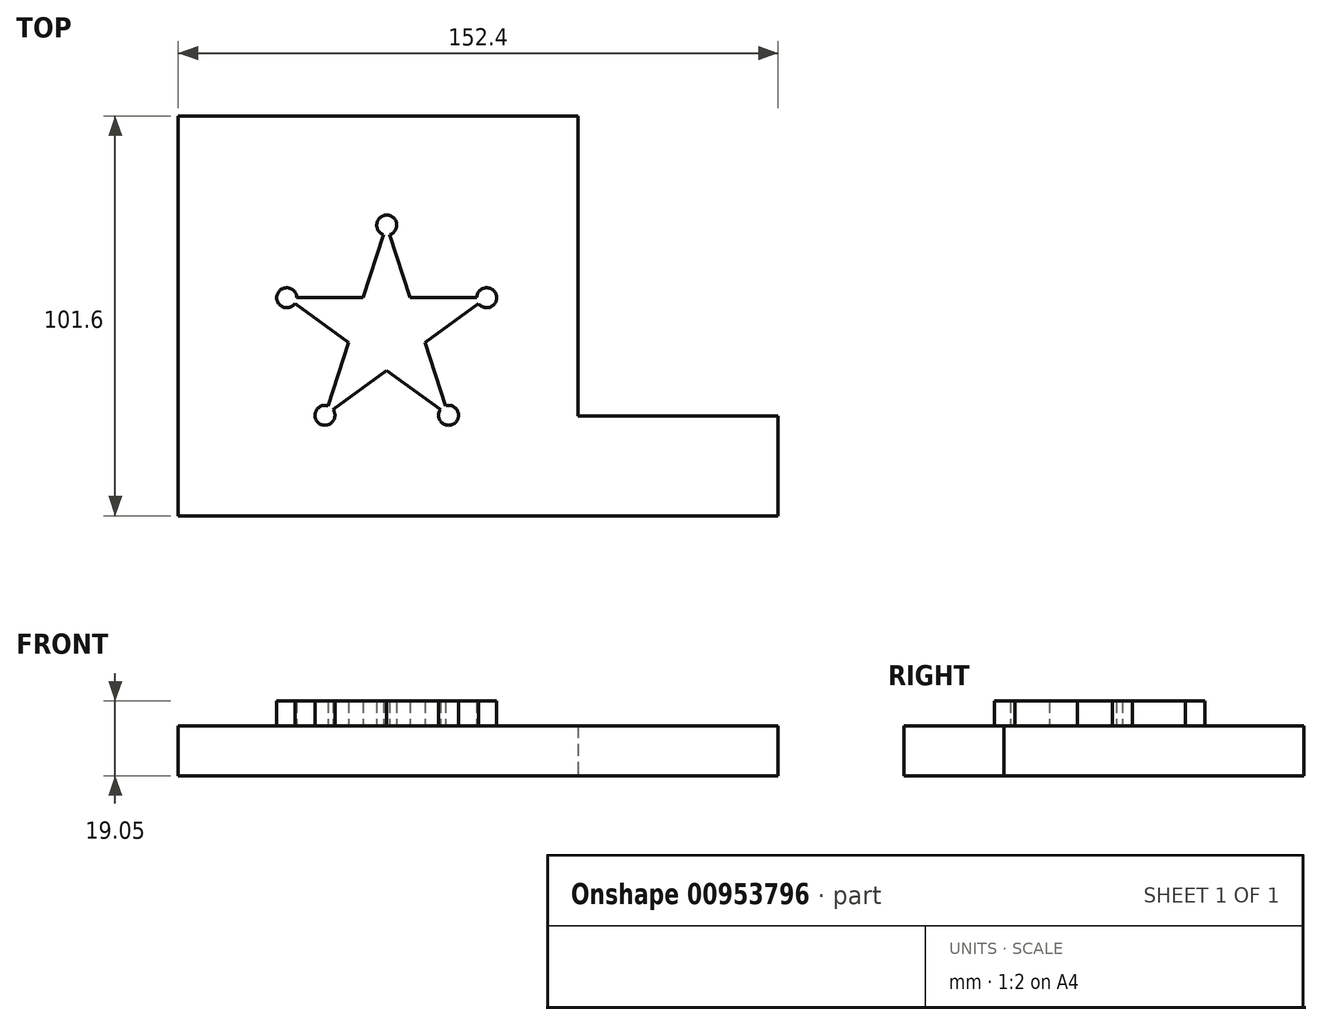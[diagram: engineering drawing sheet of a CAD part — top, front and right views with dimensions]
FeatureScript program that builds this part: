
annotation { "Feature Type Name" : "Feature", "Feature Type Description" : "" }
export const myFeature = defineFeature(function(context is Context, id is Id, definition is map)
    precondition{}
    {
        {
            var Q0;
            Q0=qCreatedBy(makeId("Top.planeOp"),FACE);
            var sketch = newSketch(context, id + "F0", { "sketchPlane" : qUnion([Q0])});
            skLineSegment(sketch, "E0", {"start": v(0, 0) * mm, "end": v(152.4, 0) * mm});
            skLineSegment(sketch, "E1", {"start": v(152.4, 0) * mm, "end": v(152.4, 25.4) * mm});
            skLineSegment(sketch, "E2", {"start": v(152.4, 25.4) * mm, "end": v(101.6, 25.4) * mm});
            skLineSegment(sketch, "E3", {"start": v(101.6, 25.4) * mm, "end": v(101.6, 101.6) * mm});
            skLineSegment(sketch, "E4", {"start": v(101.6, 101.6) * mm, "end": v(0, 101.6) * mm});
            skLineSegment(sketch, "E5", {"start": v(0, 101.6) * mm, "end": v(0, 0) * mm});
            skLineSegment(sketch, "E6.bottom", {"start": v(0, 101.6) * mm, "end": v(76.2, 101.6) * mm});
            skLineSegment(sketch, "E6.left", {"start": v(0, 101.6) * mm, "end": v(0, 76.2) * mm});
            skLineSegment(sketch, "E7", {"start": v(27.57, 55.42) * mm, "end": v(78.37, 55.42) * mm});
            skLineSegment(sketch, "E8", {"start": v(78.37, 55.42) * mm, "end": v(37.27, 25.56) * mm});
            skLineSegment(sketch, "E9", {"start": v(37.27, 25.56) * mm, "end": v(52.97, 73.88) * mm});
            skPoint(sketch, "E9.endSnap0", {"position": v(52.97, 55.42) * mm});
            skLineSegment(sketch, "E10", {"start": v(52.97, 73.88) * mm, "end": v(68.67, 25.56) * mm});
            skLineSegment(sketch, "E11", {"start": v(68.67, 25.56) * mm, "end": v(27.57, 55.42) * mm});
            skCircle(sketch, "E12", {"center": v(37.27, 25.56) * mm, "radius": 2.54 * mm});
            skCircle(sketch, "E13", {"center": v(68.67, 25.56) * mm, "radius": 2.54 * mm});
            skCircle(sketch, "E14", {"center": v(78.37, 55.42) * mm, "radius": 2.54 * mm});
            skCircle(sketch, "E15", {"center": v(52.97, 73.88) * mm, "radius": 2.54 * mm});
            skCircle(sketch, "E16", {"center": v(27.57, 55.42) * mm, "radius": 2.54 * mm});
            skPoint(sketch, "E17", {"position": v(25.4, 101.6) * mm});
            skPoint(sketch, "E18", {"position": v(50.8, 101.6) * mm});
            skPoint(sketch, "E19", {"position": v(25.4, 0) * mm});
            skPoint(sketch, "E20", {"position": v(50.8, 0) * mm});
            skPoint(sketch, "E21", {"position": v(76.2, 0) * mm});
            skPoint(sketch, "E22", {"position": v(101.6, 0) * mm});
            skPoint(sketch, "E23", {"position": v(127, 0) * mm});
            skSolve(sketch);
        }
        {
            var Q0;
            {var subQ0=sQuery(id+"F0.wireOp",EDGE,"E16");var subQ1=sQuery(id+"F0.wireOp",EDGE,"E7");var subQ2=makeQuery(id+"F0.imprint","INTERSECT",VERTEX,{"derivedFrom":[subQ1,subQ0]});Q0=makeQuery(id+"F0.imprint","IMPRINT",FACE,{"disambiguationData":[TD([[makeQuery(id+"F0.imprint","IMPRINT",EDGE,{"disambiguationData":[TD([[subQ2,-1.0]])],"derivedFrom":subQ1}),-1.0]])]});}
            var Q1;
            {var subQ1=sQuery(id+"F0.wireOp",EDGE,"E7");var subQ5=sQuery(id+"F0.wireOp",EDGE,"E9");var subQ6=makeQuery(id+"F0.imprint","INTERSECT",VERTEX,{"derivedFrom":[subQ1,subQ5]});Q1=makeQuery(id+"F0.imprint","IMPRINT",FACE,{"disambiguationData":[TD([[makeQuery(id+"F0.imprint","IMPRINT",EDGE,{"disambiguationData":[TD([[subQ6,-1.0]])],"derivedFrom":subQ1}),-1.0]])]});}
            var Q2;
            {var subQ0=sQuery(id+"F0.wireOp",EDGE,"E11");var subQ1=sQuery(id+"F0.wireOp",EDGE,"E8");var subQ2=makeQuery(id+"F0.imprint","INTERSECT",VERTEX,{"derivedFrom":[subQ1,subQ0]});Q2=makeQuery(id+"F0.imprint","IMPRINT",FACE,{"disambiguationData":[TD([[makeQuery(id+"F0.imprint","IMPRINT",EDGE,{"disambiguationData":[TD([[subQ2,-1.0]])],"derivedFrom":subQ1}),-1.0]])]});}
            var Q3;
            {var subQ0=sQuery(id+"F0.wireOp",EDGE,"E10");var subQ1=sQuery(id+"F0.wireOp",EDGE,"E8");var subQ2=makeQuery(id+"F0.imprint","INTERSECT",VERTEX,{"derivedFrom":[subQ1,subQ0]});Q3=makeQuery(id+"F0.imprint","IMPRINT",FACE,{"disambiguationData":[TD([[makeQuery(id+"F0.imprint","IMPRINT",EDGE,{"disambiguationData":[TD([[subQ2,-1.0]])],"derivedFrom":subQ1}),1.0]])]});}
            var Q4;
            {var subQ0=sQuery(id+"F0.wireOp",EDGE,"E10");var subQ1=sQuery(id+"F0.wireOp",EDGE,"E7");var subQ2=makeQuery(id+"F0.imprint","INTERSECT",VERTEX,{"derivedFrom":[subQ1,subQ0]});Q4=makeQuery(id+"F0.imprint","IMPRINT",FACE,{"disambiguationData":[TD([[makeQuery(id+"F0.imprint","IMPRINT",EDGE,{"disambiguationData":[TD([[subQ2,-1.0]])],"derivedFrom":subQ1}),-1.0]])]});}
            var Q5;
            {var subQ0=sQuery(id+"F0.wireOp",EDGE,"E9");var subQ1=sQuery(id+"F0.wireOp",EDGE,"E7");var subQ2=makeQuery(id+"F0.imprint","INTERSECT",VERTEX,{"derivedFrom":[subQ1,subQ0]});Q5=makeQuery(id+"F0.imprint","IMPRINT",FACE,{"disambiguationData":[TD([[makeQuery(id+"F0.imprint","IMPRINT",EDGE,{"disambiguationData":[TD([[subQ2,-1.0]])],"derivedFrom":subQ1}),1.0]])]});}
            var Q6;
            {var subQ0=sQuery(id+"F0.wireOp",EDGE,"E10");var subQ1=sQuery(id+"F0.wireOp",EDGE,"E9");var subQ2=makeQuery(id+"F0.imprint","INTERSECT",VERTEX,{"derivedFrom":[subQ1,subQ0]});Q6=makeQuery(id+"F0.imprint","IMPRINT",FACE,{"disambiguationData":[TD([[makeQuery(id+"F0.imprint","IMPRINT",EDGE,{"disambiguationData":[TD([[subQ2,1.0]])],"derivedFrom":subQ1}),1.0]])]});}
            var Q7;
            {var subQ0=sQuery(id+"F0.wireOp",EDGE,"E11");var subQ1=sQuery(id+"F0.wireOp",EDGE,"E7");var subQ2=makeQuery(id+"F0.imprint","INTERSECT",VERTEX,{"derivedFrom":[subQ1,subQ0]});Q7=makeQuery(id+"F0.imprint","IMPRINT",FACE,{"disambiguationData":[TD([[makeQuery(id+"F0.imprint","IMPRINT",EDGE,{"disambiguationData":[TD([[subQ2,-1.0]])],"derivedFrom":subQ1}),1.0]])]});}
            var Q8;
            {var subQ0=sQuery(id+"F0.wireOp",EDGE,"E11");var subQ1=sQuery(id+"F0.wireOp",EDGE,"E7");var subQ2=makeQuery(id+"F0.imprint","INTERSECT",VERTEX,{"derivedFrom":[subQ1,subQ0]});Q8=makeQuery(id+"F0.imprint","IMPRINT",FACE,{"disambiguationData":[TD([[makeQuery(id+"F0.imprint","IMPRINT",EDGE,{"disambiguationData":[TD([[subQ2,-1.0]])],"derivedFrom":subQ1}),-1.0]])]});}
            var Q9;
            {var subQ0=sQuery(id+"F0.wireOp",EDGE,"E10");var subQ1=sQuery(id+"F0.wireOp",EDGE,"E9");var subQ2=makeQuery(id+"F0.imprint","INTERSECT",VERTEX,{"derivedFrom":[subQ1,subQ0]});Q9=makeQuery(id+"F0.imprint","IMPRINT",FACE,{"disambiguationData":[TD([[makeQuery(id+"F0.imprint","IMPRINT",EDGE,{"disambiguationData":[TD([[subQ2,1.0]])],"derivedFrom":subQ1}),-1.0]])]});}
            var Q10;
            {var subQ0=sQuery(id+"F0.wireOp",EDGE,"E8");var subQ1=sQuery(id+"F0.wireOp",EDGE,"E7");var subQ2=makeQuery(id+"F0.imprint","INTERSECT",VERTEX,{"derivedFrom":[subQ1,subQ0]});Q10=makeQuery(id+"F0.imprint","IMPRINT",FACE,{"disambiguationData":[TD([[makeQuery(id+"F0.imprint","IMPRINT",EDGE,{"disambiguationData":[TD([[subQ2,1.0]])],"derivedFrom":subQ1}),-1.0]])]});}
            var Q11;
            {var subQ0=sQuery(id+"F0.wireOp",EDGE,"E8");var subQ1=sQuery(id+"F0.wireOp",EDGE,"E7");var subQ2=makeQuery(id+"F0.imprint","INTERSECT",VERTEX,{"derivedFrom":[subQ1,subQ0]});Q11=makeQuery(id+"F0.imprint","IMPRINT",FACE,{"disambiguationData":[TD([[makeQuery(id+"F0.imprint","IMPRINT",EDGE,{"disambiguationData":[TD([[subQ2,1.0]])],"derivedFrom":subQ1}),1.0]])]});}
            var Q12;
            {var subQ0=sQuery(id+"F0.wireOp",EDGE,"E11");var subQ1=sQuery(id+"F0.wireOp",EDGE,"E10");var subQ2=makeQuery(id+"F0.imprint","INTERSECT",VERTEX,{"derivedFrom":[subQ1,subQ0]});Q12=makeQuery(id+"F0.imprint","IMPRINT",FACE,{"disambiguationData":[TD([[makeQuery(id+"F0.imprint","IMPRINT",EDGE,{"disambiguationData":[TD([[subQ2,1.0]])],"derivedFrom":subQ1}),-1.0]])]});}
            var Q13;
            {var subQ0=sQuery(id+"F0.wireOp",EDGE,"E11");var subQ1=sQuery(id+"F0.wireOp",EDGE,"E10");var subQ2=makeQuery(id+"F0.imprint","INTERSECT",VERTEX,{"derivedFrom":[subQ1,subQ0]});Q13=makeQuery(id+"F0.imprint","IMPRINT",FACE,{"disambiguationData":[TD([[makeQuery(id+"F0.imprint","IMPRINT",EDGE,{"disambiguationData":[TD([[subQ2,1.0]])],"derivedFrom":subQ1}),1.0]])]});}
            var Q14;
            {var subQ0=sQuery(id+"F0.wireOp",EDGE,"E9");var subQ1=sQuery(id+"F0.wireOp",EDGE,"E8");var subQ2=makeQuery(id+"F0.imprint","INTERSECT",VERTEX,{"derivedFrom":[subQ1,subQ0]});Q14=makeQuery(id+"F0.imprint","IMPRINT",FACE,{"disambiguationData":[TD([[makeQuery(id+"F0.imprint","IMPRINT",EDGE,{"disambiguationData":[TD([[subQ2,1.0]])],"derivedFrom":subQ1}),-1.0]])]});}
            var Q15;
            {var subQ0=sQuery(id+"F0.wireOp",EDGE,"E9");var subQ1=sQuery(id+"F0.wireOp",EDGE,"E8");var subQ2=makeQuery(id+"F0.imprint","INTERSECT",VERTEX,{"derivedFrom":[subQ1,subQ0]});Q15=makeQuery(id+"F0.imprint","IMPRINT",FACE,{"disambiguationData":[TD([[makeQuery(id+"F0.imprint","IMPRINT",EDGE,{"disambiguationData":[TD([[subQ2,1.0]])],"derivedFrom":subQ1}),1.0]])]});}
            extrude(context, id + "F1", {"entities" : qUnion([Q0, Q1, Q2, Q3, Q4, Q5, Q6, Q7, Q8, Q9, Q10, Q11, Q12, Q13, Q14, Q15]), "depth" : 19.05 * mm, "offsetDistance" : 25.4 * mm});
        }
        {
            var Q0;
            Q0=makeQuery(id+"F0.imprint","IMPRINT",FACE,{"disambiguationData":[TD([[makeQuery(id+"F0.imprint","IMPRINT",EDGE,{"derivedFrom":sQuery(id+"F0.wireOp",EDGE,"E0")}),1.0]])]});
            extrude(context, id + "F2", {"entities" : qUnion([Q0]), "operationType" : NewBodyOperationType.ADD, "depth" : 12.7 * mm, "offsetDistance" : 25.4 * mm});
        }
    });
